# Revit family: Urinal_Siphon-Top_Spud-American_Standard-Trimbook-6561.017
name_source: partatom
category: Plumbing Fixtures
units: mm (PartAtom-declared; Revit-internal decimal feet)

## family parameters
Cut with Voids When Loaded = No
Host = Face
OmniClass Number = 23.45.05.21.11.21
OmniClass Title = Urinals
Part Type = Normal
Room Calculation Point = No
Round Connector Dimension = Use Diameter
Shared = Yes

## types (1)
- 6561017.020
    6045.101.002 - American Standard Manual (Top Spud) = No
    6063.101.002 - American Standard Selectronic® DC Power (Top Spud) = No
    ADA Compliant = Yes
    Assembly Code = D2010210
    CW Connection = Yes
    CWFU = 5
    Cold Water Connection Diameter = 3/4"
    Default Elevation = 17"
    Description = Trimbrook™ 1.0 gpf/3.8 Lpf Top Spud Siphon Jet Urinal
    Finish = Vitreous China-American Standard-020-White
    Flush Rate = 3.8 Lpf/1.0 gpf
    HW Connection = No
    HWFU = 0
    Height = 26 3/4"
    IAPMO Compliance = ASME A112.19.2-2008/CSA B45.1-08 for Vitreous China Fixtures
    Installation Type = Wall Mounted
    Length = 14"
    Manufacturer = American Standard
    Material = Vitreous China-American Standard-020-White
    Model = 6561017.020
    Product Documentation Link = https://americanstandard.box.com
    Product Page URL = https://www.americanstandard-us.com
    Revised Date = 06/23/2022
    URL = http://www.americanstandard-us.com
    Vent Connection = No
    WFU = 5
    Waste Connection = Yes
    Waste Connection Diameter = 2"
    Width = 17 1/2"

## geometry (parser evidence)
native form markers: Sweep x2
no freeform markers — native parametric forms only
